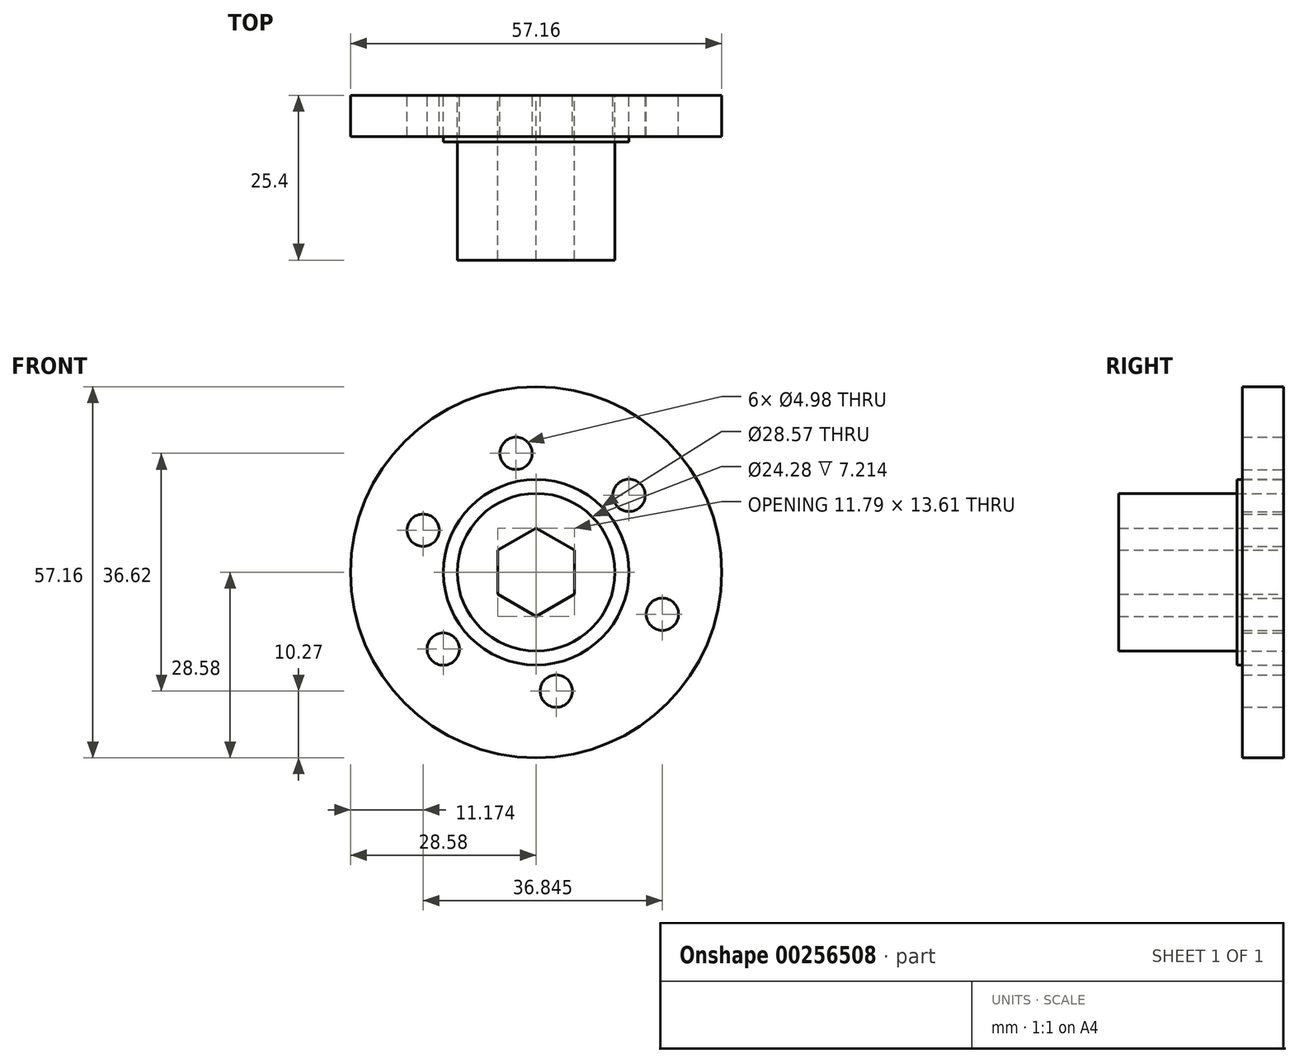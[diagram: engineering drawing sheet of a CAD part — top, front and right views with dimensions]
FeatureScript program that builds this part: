
annotation { "Feature Type Name" : "Feature", "Feature Type Description" : "" }
export const myFeature = defineFeature(function(context is Context, id is Id, definition is map)
    precondition{}
    {
        {
            var Q0;
            Q0=qCreatedBy(makeId("Front.planeOp"),FACE);
            var sketch = newSketch(context, id + "F0", { "sketchPlane" : qUnion([Q0])});
            skCircle(sketch, "E0", {"center": v(0, 0) * mm, "radius": 28.57 * mm});
            skPoint(sketch, "E1.0.midPoint", {"position": v(15.86, 2.68) * mm});
            skCircle(sketch, "E2", {"center": v(-3.1, 18.3) * mm, "radius": 2.49 * mm});
            skCircle(sketch, "E3", {"center": v(-17.4, 6.47) * mm, "radius": 2.49 * mm});
            skCircle(sketch, "E4", {"center": v(-14.3, -11.84) * mm, "radius": 2.49 * mm});
            skCircle(sketch, "E5", {"center": v(3.1, -18.3) * mm, "radius": 2.49 * mm});
            skCircle(sketch, "E6", {"center": v(19.44, -6.47) * mm, "radius": 2.49 * mm});
            skCircle(sketch, "E7", {"center": v(14.3, 11.84) * mm, "radius": 2.49 * mm});
            skPoint(sketch, "E1.1.start.orphan", {"position": v(17.4, -6.47) * mm});
            skCircle(sketch, "E8.cCircle", {"center": v(0, 0) * mm, "radius": 5.9 * mm, "construction": true});
            skLineSegment(sketch, "E8.0", {"start": v(5.9, 3.4) * mm, "end": v(5.9, -3.4) * mm});
            skLineSegment(sketch, "E8.1", {"start": v(5.9, -3.4) * mm, "end": v(0, -6.8) * mm});
            skLineSegment(sketch, "E8.2", {"start": v(0, -6.8) * mm, "end": v(-5.9, -3.4) * mm});
            skLineSegment(sketch, "E8.3", {"start": v(-5.9, -3.4) * mm, "end": v(-5.9, 3.4) * mm});
            skLineSegment(sketch, "E8.4", {"start": v(-5.9, 3.4) * mm, "end": v(0, 6.8) * mm});
            skLineSegment(sketch, "E8.5", {"start": v(0, 6.8) * mm, "end": v(5.9, 3.4) * mm});
            skPoint(sketch, "E8.0.midPoint", {"position": v(5.9, 0) * mm});
            skCircle(sketch, "E9", {"center": v(0, 0) * mm, "radius": 14.29 * mm});
            skCircle(sketch, "E10", {"center": v(0, 0) * mm, "radius": 12.14 * mm});
            skSolve(sketch);
        }
        {
            var Q0;
            Q0=makeQuery(id+"F0.imprint","IMPRINT",FACE,{"disambiguationData":[TD([[makeQuery(id+"F0.imprint","IMPRINT",EDGE,{"derivedFrom":sQuery(id+"F0.wireOp",EDGE,"E8.0")}),1.0]])]});
            extrude(context, id + "F1", {"entities" : qUnion([Q0]), "depth" : 25.4 * mm});
        }
        {
            var Q0;
            Q0 = qSketchRegion(id + "F0", true);
            extrude(context, id + "F2", {"entities" : qUnion([Q0]), "depth" : 6.35 * mm});
        }
        {
            var Q0;
            Q0=makeQuery(id+"F0.imprint","IMPRINT",FACE,{"disambiguationData":[TD([[makeQuery(id+"F0.imprint","IMPRINT",EDGE,{"derivedFrom":sQuery(id+"F0.wireOp",EDGE,"E9")}),1.0]])]});
            extrude(context, id + "F3", {"entities" : qUnion([Q0]), "depth" : 7.2 * mm});
        }
    });
